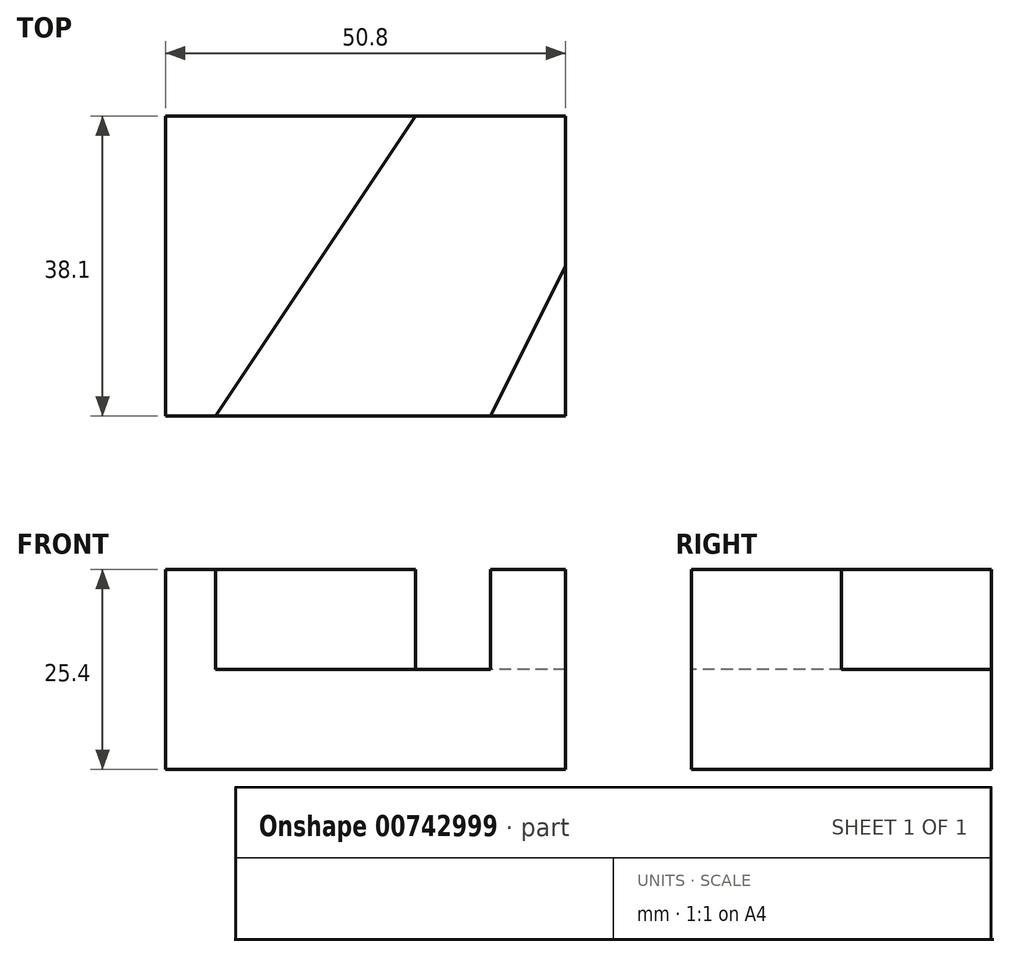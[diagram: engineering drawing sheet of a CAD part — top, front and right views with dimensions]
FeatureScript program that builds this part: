
annotation { "Feature Type Name" : "Feature", "Feature Type Description" : "" }
export const myFeature = defineFeature(function(context is Context, id is Id, definition is map)
    precondition{}
    {
        {
            var Q0;
            Q0=qCreatedBy(makeId("Front.planeOp"),FACE);
            var sketch = newSketch(context, id + "F0", { "sketchPlane" : qUnion([Q0])});
            skLineSegment(sketch, "E0", {"start": v(0, 0) * mm, "end": v(0, 25.4) * mm});
            skLineSegment(sketch, "E1", {"start": v(0, 25.4) * mm, "end": v(50.8, 25.4) * mm});
            skLineSegment(sketch, "E2", {"start": v(50.8, 25.4) * mm, "end": v(50.8, 0) * mm});
            skLineSegment(sketch, "E3", {"start": v(50.8, 0) * mm, "end": v(0, 0) * mm});
            skSolve(sketch);
        }
        {
            var Q0;
            Q0 = qSketchRegion(id + "F0", true);
            extrude(context, id + "F1", {"entities" : qUnion([Q0]), "depth" : 38.1 * mm, "offsetDistance" : 25.4 * mm});
        }
        {
            var Q0;
            Q0=makeQuery(id+"F1.opExtrude","SWEPT_FACE",FACE,{"disambiguationData":[OSD([sQuery(id+"F0.wireOp",EDGE,"E2")])]});
            var sketch = newSketch(context, id + "F2", { "sketchPlane" : qUnion([Q0])});
            skLineSegment(sketch, "E4.bottom", {"start": v(-19.05, 25.4) * mm, "end": v(0, 25.4) * mm});
            skLineSegment(sketch, "E4.top", {"start": v(-19.05, 12.7) * mm, "end": v(0, 12.7) * mm});
            skLineSegment(sketch, "E4.left", {"start": v(-19.05, 25.4) * mm, "end": v(-19.05, 12.7) * mm});
            skLineSegment(sketch, "E4.right", {"start": v(0, 25.4) * mm, "end": v(0, 12.7) * mm});
            skSolve(sketch);
        }
        {
            var Q0;
            Q0=makeQuery(id+"F2.imprint","IMPRINT",FACE,{"disambiguationData":[TD([[makeQuery(id+"F2.imprint","IMPRINT",EDGE,{"derivedFrom":sQuery(id+"F2.wireOp",EDGE,"E4.bottom")}),-1.0]])]});
            extrude(context, id + "F3", {"entities" : qUnion([Q0]), "operationType" : NewBodyOperationType.REMOVE, "oppositeDirection" : true, "depth" : 19.05 * mm, "offsetDistance" : 25.4 * mm});
        }
        {
            var Q0;
            Q0=makeQuery(id+"F1.opExtrude","SWEPT_FACE",FACE,{"disambiguationData":[OSD([sQuery(id+"F0.wireOp",EDGE,"E1")])]});
            var sketch = newSketch(context, id + "F4", { "sketchPlane" : qUnion([Q0])});
            skLineSegment(sketch, "E5", {"start": v(50.8, -19.05) * mm, "end": v(41.27, -38.1) * mm});
            skPoint(sketch, "E5.endSnap0", {"position": v(41.27, -19.05) * mm});
            skLineSegment(sketch, "E6", {"start": v(31.75, 0) * mm, "end": v(6.35, -38.1) * mm});
            skSolve(sketch);
        }
        {
            var Q0;
            Q0 = qSketchRegion(id + "F4", true);
            var Q1;
            {var subQ3=sQuery(id+"F4.wireOp",EDGE,"E5");Q1=makeQuery(id+"F4.imprint","IMPRINT",FACE,{"disambiguationData":[TD([[makeQuery(id+"F4.imprint","IMPRINT",EDGE,{"derivedFrom":subQ3}),-1.0]])]});}
            extrude(context, id + "F5", {"entities" : qUnion([Q0, Q1]), "operationType" : NewBodyOperationType.REMOVE, "oppositeDirection" : true, "depth" : 12.7 * mm, "offsetDistance" : 25.4 * mm});
        }
    });
